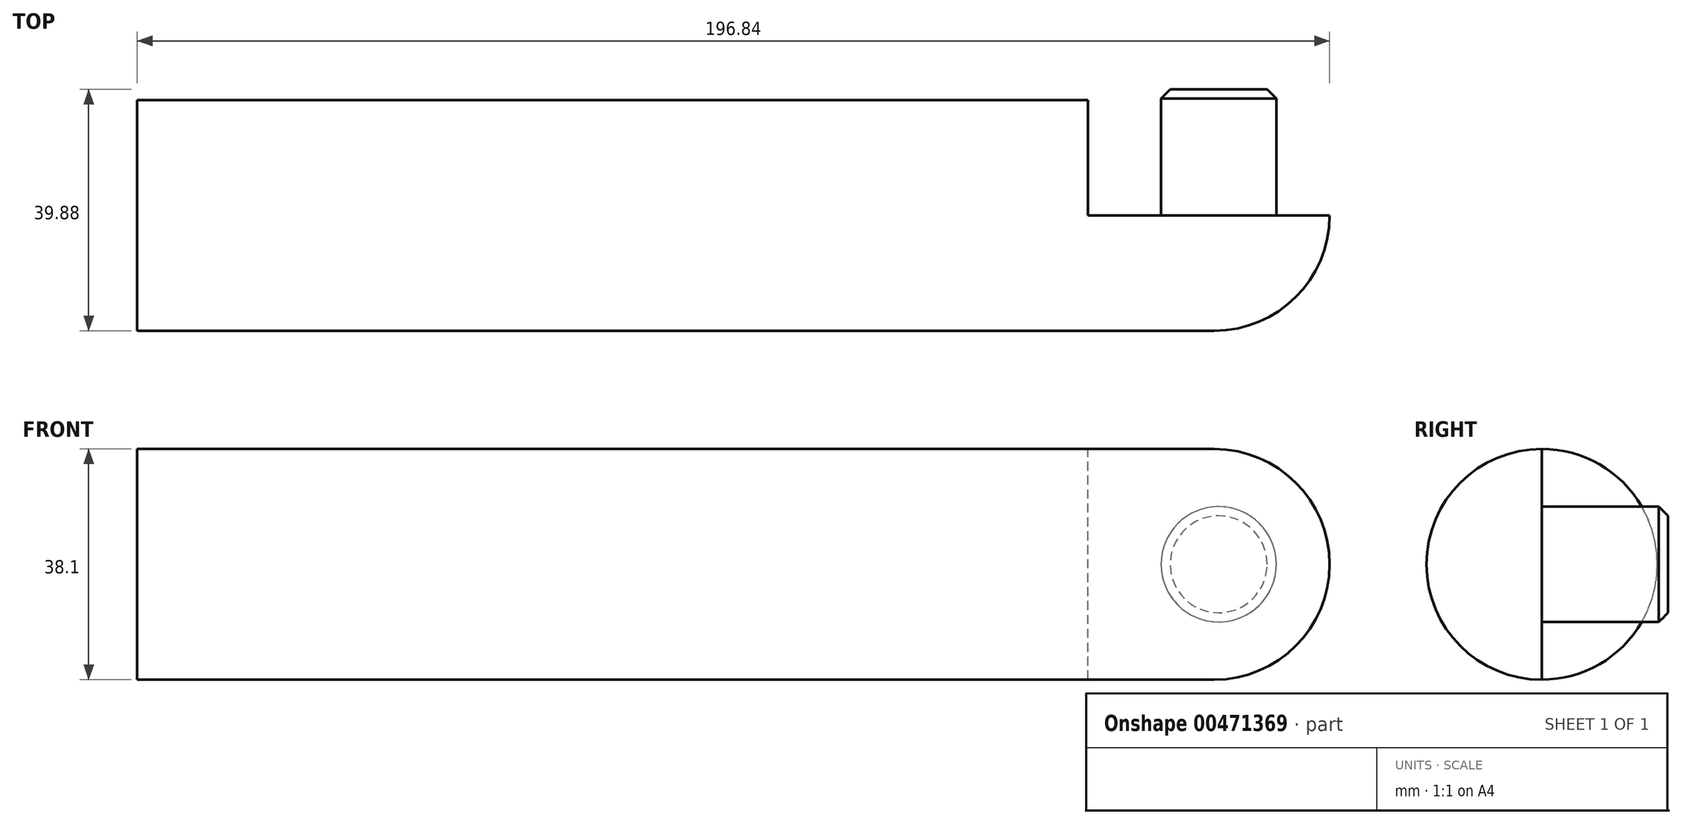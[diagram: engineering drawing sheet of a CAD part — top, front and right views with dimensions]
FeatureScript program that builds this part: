
annotation { "Feature Type Name" : "Feature", "Feature Type Description" : "" }
export const myFeature = defineFeature(function(context is Context, id is Id, definition is map)
    precondition{}
    {
        {
            var Q0;
            Q0=qCreatedBy(makeId("Front.planeOp"),FACE);
            var sketch = newSketch(context, id + "F0", { "sketchPlane" : qUnion([Q0])});
            skLineSegment(sketch, "E0.bottom", {"start": v(28.75, 19.05) * mm, "end": v(-128.22, 19.05) * mm});
            skLineSegment(sketch, "E0.top", {"start": v(28.75, -19.05) * mm, "end": v(-128.22, -19.05) * mm});
            skLineSegment(sketch, "E0.left", {"start": v(28.75, 19.05) * mm, "end": v(28.75, -19.05) * mm});
            skLineSegment(sketch, "E0.right", {"start": v(-128.22, 19.05) * mm, "end": v(-128.22, -19.05) * mm});
            skPoint(sketch, "E0.middle", {"position": v(-49.74, 0) * mm});
            skLineSegment(sketch, "E1", {"start": v(28.75, 0) * mm, "end": v(-128.22, 0) * mm});
            skSolve(sketch);
        }
        {
            var Q0;
            Q0=qCreatedBy(makeId("Front.planeOp"),FACE);
            var sketch = newSketch(context, id + "F1", { "sketchPlane" : qUnion([Q0])});
            skLineSegment(sketch, "E2", {"start": v(28.75, 19.05) * mm, "end": v(49.58, 19.05) * mm});
            skLineSegment(sketch, "E3", {"start": v(28.75, -19.05) * mm, "end": v(49.58, -19.05) * mm});
            skLineSegment(sketch, "E4", {"start": v(49.58, 19.05) * mm, "end": v(49.58, -19.05) * mm});
            skLineSegment(sketch, "E5", {"start": v(28.75, 0) * mm, "end": v(49.58, 0) * mm});
            skLineSegment(sketch, "E6.0", {"start": v(28.75, 19.05) * mm, "end": v(28.75, -19.05) * mm});
            skSolve(sketch);
        }
        {
            var Q0;
            Q0=qCreatedBy(makeId("Front.planeOp"),FACE);
            var sketch = newSketch(context, id + "F2", { "sketchPlane" : qUnion([Q0])});
            skCircle(sketch, "E7", {"center": v(50.32, 0) * mm, "radius": 9.53 * mm});
            skSolve(sketch);
        }
        {
            var Q0;
            {var subQ0=sQuery(id+"F0.wireOp",EDGE,"E0.bottom");Q0=makeQuery(id+"F0.imprint","IMPRINT",FACE,{"disambiguationData":[TD([[makeQuery(id+"F0.imprint","IMPRINT",EDGE,{"derivedFrom":subQ0}),1.0]])]});}
            var Q1;
            Q1=sQuery(id+"F0.wireOp",EDGE,"E1");
            revolve(context, id + "F3", {"entities" : qUnion([Q0]), "axis" : qUnion([Q1]), "revolveType" : RevolveType.FULL});
        }
        {
            var Q0;
            {var subQ0=sQuery(id+"F1.wireOp",EDGE,"E2");Q0=makeQuery(id+"F1.imprint","IMPRINT",FACE,{"disambiguationData":[TD([[makeQuery(id+"F1.imprint","IMPRINT",EDGE,{"derivedFrom":subQ0}),-1.0]])]});}
            var Q1;
            Q1=sQuery(id+"F1.wireOp",EDGE,"E5");
            revolve(context, id + "F4", {"operationType" : NewBodyOperationType.ADD, "entities" : qUnion([Q0]), "axis" : qUnion([Q1]), "revolveType" : RevolveType.ONE_DIRECTION, "angle" : 180 * degree});
        }
        {
            var Q0;
            Q0=makeQuery(id+"F4.opRevolve","SWEPT_FACE",FACE,{"disambiguationData":[OSD([sQuery(id+"F1.wireOp",EDGE,"E4")])]});
            var Q1;
            Q1=sQuery(id+"F1.wireOp",EDGE,"E4");
            revolve(context, id + "F5", {"operationType" : NewBodyOperationType.ADD, "entities" : qUnion([Q0]), "axis" : qUnion([Q1]), "revolveType" : RevolveType.ONE_DIRECTION, "oppositeDirection" : true, "angle" : 90 * degree});
        }
        {
            var Q0;
            Q0=makeQuery(id+"F2.imprint","IMPRINT",FACE,{"disambiguationData":[TD([[makeQuery(id+"F2.imprint","IMPRINT",EDGE,{"derivedFrom":sQuery(id+"F2.wireOp",EDGE,"E7")}),1.0]])]});
            extrude(context, id + "F6", {"entities" : qUnion([Q0]), "operationType" : NewBodyOperationType.ADD, "oppositeDirection" : true, "depth" : 20.83 * mm});
        }
        {
            var Q0;
            Q0=makeQuery(id+"F6.opExtrude","CAP_FACE",FACE,{"disambiguationData":[OSD([sQuery(id+"F2.wireOp",EDGE,"E7")])],"isStart":false});
            chamfer(context, id + "F7", {"entities" : qUnion([Q0]), "chamferType" : ChamferType.OFFSET_ANGLE, "width" : 1.52 * mm, "oppositeDirection" : true, "angle" : 45 * degree, "tangentPropagation" : true});
        }
    });
